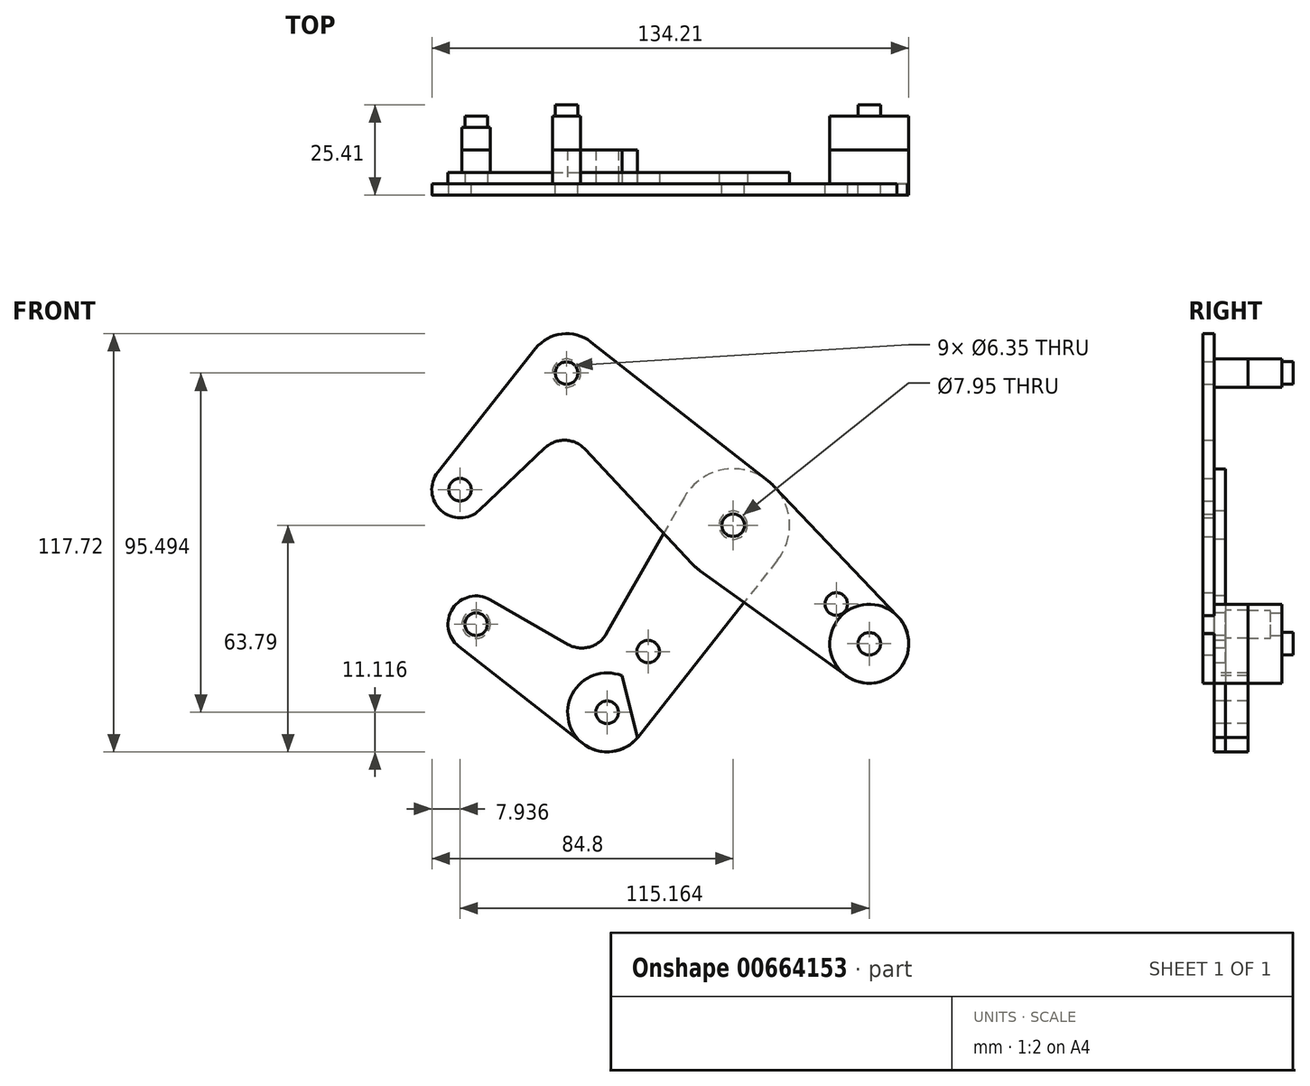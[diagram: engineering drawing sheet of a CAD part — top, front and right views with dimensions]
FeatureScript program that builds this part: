
annotation { "Feature Type Name" : "Feature", "Feature Type Description" : "" }
export const myFeature = defineFeature(function(context is Context, id is Id, definition is map)
    precondition{}
    {
        {
            var Q0;
            Q0=qCreatedBy(makeId("Front.planeOp"),FACE);
            var sketch = newSketch(context, id + "F0", { "sketchPlane" : qUnion([Q0])});
            skCircle(sketch, "E0", {"center": v(0, 0) * mm, "radius": 15.88 * mm});
            skCircle(sketch, "E1", {"center": v(-46.9, 42.82) * mm, "radius": 11.11 * mm});
            skCircle(sketch, "E2", {"center": v(-76.86, 10) * mm, "radius": 7.94 * mm});
            skCircle(sketch, "E3", {"center": v(38.3, -33.37) * mm, "radius": 11.11 * mm});
            skLineSegment(sketch, "E4", {"start": v(-46.9, 42.82) * mm, "end": v(37.51, -34.26) * mm, "construction": true});
            skLineSegment(sketch, "E5", {"start": v(-46.9, 42.82) * mm, "end": v(-76.86, 10) * mm, "construction": true});
            skCircle(sketch, "E6", {"center": v(0, 0) * mm, "radius": 3.98 * mm});
            skCircle(sketch, "E7", {"center": v(0, 0) * mm, "radius": 3.18 * mm});
            skCircle(sketch, "E8", {"center": v(-46.9, 42.82) * mm, "radius": 3.18 * mm});
            skCircle(sketch, "E9", {"center": v(-76.86, 10) * mm, "radius": 3.18 * mm});
            skCircle(sketch, "E10", {"center": v(38.3, -33.37) * mm, "radius": 3.18 * mm});
            skCircle(sketch, "E11", {"center": v(29.01, -22.2) * mm, "radius": 3.18 * mm});
            skLineSegment(sketch, "E12", {"start": v(26.87, -24.54) * mm, "end": v(46.56, -42.52) * mm, "construction": true});
            skLineSegment(sketch, "E13", {"start": v(0, 0) * mm, "end": v(-35.46, -52.67) * mm, "construction": true});
            skCircle(sketch, "E14", {"center": v(-35.46, -52.67) * mm, "radius": 11.11 * mm});
            skCircle(sketch, "E15", {"center": v(-35.46, -52.67) * mm, "radius": 3.18 * mm});
            skLineSegment(sketch, "E16", {"start": v(-35.46, -52.67) * mm, "end": v(-72.34, -27.85) * mm, "construction": true});
            skCircle(sketch, "E17", {"center": v(-72.34, -27.85) * mm, "radius": 7.94 * mm});
            skCircle(sketch, "E18", {"center": v(-72.34, -27.85) * mm, "radius": 3.18 * mm});
            skCircle(sketch, "E19", {"center": v(-23.93, -35.54) * mm, "radius": 3.18 * mm});
            skLineSegment(sketch, "E20", {"start": v(-55.61, 49.7) * mm, "end": v(-83.1, 14.92) * mm});
            skLineSegment(sketch, "E21", {"start": v(11.5, 10.94) * mm, "end": v(46.35, -25.72) * mm});
            skLineSegment(sketch, "E22", {"start": v(31.82, -42.4) * mm, "end": v(-9.26, -12.9) * mm});
            skLineSegment(sketch, "E23", {"start": v(-11.6, -10.83) * mm, "end": v(-41.7, 21.43) * mm});
            skLineSegment(sketch, "E24", {"start": v(-71.4, 4.24) * mm, "end": v(-52.96, 21.74) * mm});
            skLineSegment(sketch, "E25", {"start": v(-40.03, 51.56) * mm, "end": v(9.8, 12.5) * mm});
            skArc(sketch, "E26", {"start": v(-41.7, 21.43) * mm, "mid": v(-47.26, 23.92) * mm, "end": v(-52.96, 21.74) * mm});
            skArc(sketch, "E27", {"start": v(-41.83, 21.56) * mm, "mid": v(-47.35, 23.93) * mm, "end": v(-52.96, 21.74) * mm});
            skLineSegment(sketch, "E28", {"start": v(-52.96, 21.74) * mm, "end": v(-52.91, 21.78) * mm});
            skLineSegment(sketch, "E29", {"start": v(-41.7, 21.43) * mm, "end": v(-41.7, 21.43) * mm});
            skLineSegment(sketch, "E30.trimOffspring", {"start": v(-54.4, 34.6) * mm, "end": v(-54.98, 35.2) * mm});
            skPoint(sketch, "E31", {"position": v(-52.96, 21.74) * mm});
            skPoint(sketch, "E32", {"position": v(-41.7, 21.43) * mm});
            skLineSegment(sketch, "E33", {"start": v(-77.23, -34.1) * mm, "end": v(-42.31, -61.42) * mm});
            skLineSegment(sketch, "E34", {"start": v(12.47, -9.83) * mm, "end": v(-26.74, -59.55) * mm});
            skLineSegment(sketch, "E35", {"start": v(26.87, -24.54) * mm, "end": v(29.01, -22.2) * mm, "construction": true});
            skLineSegment(sketch, "E36", {"start": v(-11.72, 10.7) * mm, "end": v(-11.94, 10.47) * mm});
            skPoint(sketch, "E37.orphan", {"position": v(-90.16, -4.57) * mm});
            skLineSegment(sketch, "E38", {"start": v(-68.38, -20.96) * mm, "end": v(-46.52, -33.51) * mm});
            skLineSegment(sketch, "E39", {"start": v(-13.8, 7.85) * mm, "end": v(-35.66, -30.55) * mm});
            skArc(sketch, "E40", {"start": v(-46.52, -33.51) * mm, "mid": v(-40.48, -34.29) * mm, "end": v(-35.66, -30.55) * mm});
            skLineSegment(sketch, "E41.trimOffspring", {"start": v(-44.7, -46.45) * mm, "end": v(-45.12, -47.18) * mm});
            skLineSegment(sketch, "E42.trimOffspring", {"start": v(-29.93, -43.04) * mm, "end": v(-29.24, -43.43) * mm});
            skSolve(sketch);
        }
        {
            var Q0;
            {var subQ5=sQuery(id+"F0.wireOp",EDGE,"E20");Q0=makeQuery(id+"F0.imprint","IMPRINT",FACE,{"disambiguationData":[TD([[makeQuery(id+"F0.imprint","IMPRINT",EDGE,{"derivedFrom":subQ5}),1.0]])]});}
            var Q1;
            Q1=makeQuery(id+"F0.imprint","IMPRINT",FACE,{"disambiguationData":[TD([[makeQuery(id+"F0.imprint","IMPRINT",EDGE,{"derivedFrom":sQuery(id+"F0.wireOp",EDGE,"E9")}),-1.0]])]});
            var Q2;
            Q2=makeQuery(id+"F0.imprint","IMPRINT",FACE,{"disambiguationData":[TD([[makeQuery(id+"F0.imprint","IMPRINT",EDGE,{"derivedFrom":sQuery(id+"F0.wireOp",EDGE,"E8")}),-1.0]])]});
            var Q3;
            Q3=makeQuery(id+"F0.imprint","IMPRINT",FACE,{"disambiguationData":[TD([[makeQuery(id+"F0.imprint","IMPRINT",EDGE,{"derivedFrom":sQuery(id+"F0.wireOp",EDGE,"E6")}),-1.0]])]});
            var Q4;
            {var subQ0=sQuery(id+"F0.wireOp",EDGE,"E23");var subQ1=sQuery(id+"F0.wireOp",EDGE,"E0");var subQ2=makeQuery(id+"F0.imprint","INTERSECT",VERTEX,{"derivedFrom":[subQ1,subQ0]});Q4=makeQuery(id+"F0.imprint","IMPRINT",FACE,{"disambiguationData":[TD([[makeQuery(id+"F0.imprint","IMPRINT",EDGE,{"disambiguationData":[TD([[subQ2,1.0]])],"derivedFrom":subQ1}),-1.0]])]});}
            var Q5;
            Q5=makeQuery(id+"F0.imprint","IMPRINT",FACE,{"disambiguationData":[TD([[makeQuery(id+"F0.imprint","IMPRINT",EDGE,{"derivedFrom":sQuery(id+"F0.wireOp",EDGE,"E11")}),-1.0]])]});
            var Q6;
            {var subQ0=sQuery(id+"F0.wireOp",EDGE,"E22");var subQ1=sQuery(id+"F0.wireOp",EDGE,"E0");var subQ2=makeQuery(id+"F0.imprint","INTERSECT",VERTEX,{"derivedFrom":[subQ1,subQ0]});Q6=makeQuery(id+"F0.imprint","IMPRINT",FACE,{"disambiguationData":[TD([[makeQuery(id+"F0.imprint","IMPRINT",EDGE,{"disambiguationData":[TD([[subQ2,-1.0]])],"derivedFrom":subQ1}),-1.0]])]});}
            var Q7;
            Q7=makeQuery(id+"F0.imprint","IMPRINT",FACE,{"disambiguationData":[TD([[makeQuery(id+"F0.imprint","IMPRINT",EDGE,{"derivedFrom":sQuery(id+"F0.wireOp",EDGE,"E10")}),-1.0]])]});
            var Q8;
            Q8=makeQuery(id+"F0.imprint","IMPRINT",FACE,{"disambiguationData":[TD([[makeQuery(id+"F0.imprint","IMPRINT",EDGE,{"derivedFrom":sQuery(id+"F0.wireOp",EDGE,"E6")}),1.0]])]});
            extrude(context, id + "F1", {"entities" : qUnion([Q0, Q1, Q2, Q3, Q4, Q5, Q6, Q7, Q8]), "depth" : 3.17 * mm, "offsetDistance" : 25.4 * mm});
        }
        {
            var Q0;
            Q0=makeQuery(id+"F0.imprint","IMPRINT",FACE,{"disambiguationData":[TD([[makeQuery(id+"F0.imprint","IMPRINT",EDGE,{"derivedFrom":sQuery(id+"F0.wireOp",EDGE,"E19")}),-1.0]])]});
            var Q1;
            {var subQ0=sQuery(id+"F0.wireOp",EDGE,"E22");var subQ1=sQuery(id+"F0.wireOp",EDGE,"E0");var subQ2=makeQuery(id+"F0.imprint","INTERSECT",VERTEX,{"derivedFrom":[subQ1,subQ0]});Q1=makeQuery(id+"F0.imprint","IMPRINT",FACE,{"disambiguationData":[TD([[makeQuery(id+"F0.imprint","IMPRINT",EDGE,{"disambiguationData":[TD([[subQ2,-1.0]])],"derivedFrom":subQ1}),-1.0]])]});}
            var Q2;
            {var subQ0=sQuery(id+"F0.wireOp",EDGE,"E23");var subQ1=sQuery(id+"F0.wireOp",EDGE,"E0");var subQ2=makeQuery(id+"F0.imprint","INTERSECT",VERTEX,{"derivedFrom":[subQ1,subQ0]});Q2=makeQuery(id+"F0.imprint","IMPRINT",FACE,{"disambiguationData":[TD([[makeQuery(id+"F0.imprint","IMPRINT",EDGE,{"disambiguationData":[TD([[subQ2,1.0]])],"derivedFrom":subQ1}),-1.0]])]});}
            var Q3;
            Q3=makeQuery(id+"F0.imprint","IMPRINT",FACE,{"disambiguationData":[TD([[makeQuery(id+"F0.imprint","IMPRINT",EDGE,{"derivedFrom":sQuery(id+"F0.wireOp",EDGE,"E6")}),-1.0]])]});
            var Q4;
            Q4=makeQuery(id+"F0.imprint","IMPRINT",FACE,{"disambiguationData":[TD([[makeQuery(id+"F0.imprint","IMPRINT",EDGE,{"derivedFrom":sQuery(id+"F0.wireOp",EDGE,"E15")}),-1.0]])]});
            var Q5;
            {var subQ0=sQuery(id+"F0.wireOp",EDGE,"3amZSNLC-43hP-8FI3-ZThT-5at0zfi7Zp9o");Q5=makeQuery(id+"F0.imprint","IMPRINT",FACE,{"disambiguationData":[TD([[makeQuery(id+"F0.imprint","IMPRINT",EDGE,{"derivedFrom":subQ0}),1.0]])]});}
            var Q6;
            {var subQ0=sQuery(id+"F0.wireOp",EDGE,"E33");Q6=makeQuery(id+"F0.imprint","IMPRINT",FACE,{"disambiguationData":[TD([[makeQuery(id+"F0.imprint","IMPRINT",EDGE,{"derivedFrom":subQ0}),1.0]])]});}
            var Q7;
            Q7=makeQuery(id+"F0.imprint","IMPRINT",FACE,{"disambiguationData":[TD([[makeQuery(id+"F0.imprint","IMPRINT",EDGE,{"derivedFrom":sQuery(id+"F0.wireOp",EDGE,"E18")}),-1.0]])]});
            extrude(context, id + "F2", {"entities" : qUnion([Q0, Q1, Q2, Q3, Q4, Q5, Q6, Q7]), "oppositeDirection" : true, "depth" : 3.17 * mm, "offsetDistance" : 25.4 * mm});
        }
        {
            var Q0;
            Q0=makeQuery(id+"F1.opExtrude","CAP_FACE",FACE,{"disambiguationData":[OSD([sQuery(id+"F0.wireOp",EDGE,"E0"),sQuery(id+"F0.wireOp",EDGE,"E1"),sQuery(id+"F0.wireOp",EDGE,"E2"),sQuery(id+"F0.wireOp",EDGE,"E3"),sQuery(id+"F0.wireOp",EDGE,"E7"),sQuery(id+"F0.wireOp",EDGE,"E8"),sQuery(id+"F0.wireOp",EDGE,"E9"),sQuery(id+"F0.wireOp",EDGE,"E10"),sQuery(id+"F0.wireOp",EDGE,"E11"),sQuery(id+"F0.wireOp",EDGE,"E20"),sQuery(id+"F0.wireOp",EDGE,"E21"),sQuery(id+"F0.wireOp",EDGE,"E22"),sQuery(id+"F0.wireOp",EDGE,"E23"),sQuery(id+"F0.wireOp",EDGE,"E24"),sQuery(id+"F0.wireOp",EDGE,"E25"),sQuery(id+"F0.wireOp",EDGE,"E27"),sQuery(id+"F0.wireOp",EDGE,"E28")])],"isStart":false});
            var sketch = newSketch(context, id + "F3", { "sketchPlane" : qUnion([Q0])});
            skCircle(sketch, "E43", {"center": v(-46.9, 42.82) * mm, "radius": 3.98 * mm});
            skCircle(sketch, "E44", {"center": v(0, 0) * mm, "radius": 3.98 * mm});
            skCircle(sketch, "E45", {"center": v(38.3, -33.37) * mm, "radius": 11.11 * mm});
            skSolve(sketch);
        }
        {
            var Q0;
            Q0=makeQuery(id+"F2.opExtrude","CAP_FACE",FACE,{"disambiguationData":[OSD([sQuery(id+"F0.wireOp",EDGE,"E0"),sQuery(id+"F0.wireOp",EDGE,"E6"),sQuery(id+"F0.wireOp",EDGE,"E14"),sQuery(id+"F0.wireOp",EDGE,"E15"),sQuery(id+"F0.wireOp",EDGE,"E17"),sQuery(id+"F0.wireOp",EDGE,"E18"),sQuery(id+"F0.wireOp",EDGE,"E19"),sQuery(id+"F0.wireOp",EDGE,"zHbHai0O-zoeY-vRAu-LCtb-dT5vAsICp8MH"),sQuery(id+"F0.wireOp",EDGE,"ZkpdVOQ3-HPfv-Rj2Q-2N2k-vu5tipJXAsQn"),sQuery(id+"F0.wireOp",EDGE,"E33"),sQuery(id+"F0.wireOp",EDGE,"E34"),sQuery(id+"F0.wireOp",EDGE,"qrG7Sbz3-pH1N-X5PJ-92qv-GuBl7YAv6E5Q"),sQuery(id+"F0.wireOp",EDGE,"3amZSNLC-43hP-8FI3-ZThT-5at0zfi7Zp9o")])],"isStart":true});
            var sketch = newSketch(context, id + "F4", { "sketchPlane" : qUnion([Q0])});
            skCircle(sketch, "E46", {"center": v(-35.46, -52.67) * mm, "radius": 11.11 * mm});
            skPoint(sketch, "E47", {"position": v(-29.11, -52.67) * mm});
            skLineSegment(sketch, "E48", {"start": v(-29.11, -43.55) * mm, "end": v(-29.11, -43.55) * mm});
            skCircle(sketch, "E49", {"center": v(-72.34, -27.85) * mm, "radius": 3.98 * mm});
            skLineSegment(sketch, "E50", {"start": v(-35.46, -52.67) * mm, "end": v(38.72, -33.99) * mm, "construction": true});
            skPoint(sketch, "E51", {"position": v(-29.11, -51.07) * mm});
            skLineSegment(sketch, "E52", {"start": v(-31.3, -42.37) * mm, "end": v(-29.11, -51.07) * mm});
            skLineSegment(sketch, "E53", {"start": v(-29.11, -51.07) * mm, "end": v(-26.92, -59.78) * mm});
            skSolve(sketch);
        }
        {
            var Q0;
            Q0=qCreatedBy(makeId("Front.planeOp"),FACE);
            cPlane(context, id + "F5", {"entities" : qUnion([Q0]), "cplaneType" : CPlaneType.OFFSET, "offset" : 9.52 * mm, "oppositeDirection" : true, "width" : 152.4 * mm, "height" : 152.4 * mm});
        }
        {
            var Q0;
            Q0=makeQuery(id+"F3.imprint","IMPRINT",FACE,{"disambiguationData":[TD([[makeQuery(id+"F3.imprint","IMPRINT",EDGE,{"derivedFrom":sQuery(id+"F3.wireOp",EDGE,"E43")}),1.0]])]});
            var Q1;
            Q1=makeQuery(id+"F4.imprint","IMPRINT",FACE,{"disambiguationData":[TD([[makeQuery(id+"F4.imprint","IMPRINT",EDGE,{"derivedFrom":makeQuery(id+"F2.opExtrude","CAP_EDGE",EDGE,{"disambiguationData":[OSD([sQuery(id+"F0.wireOp",EDGE,"E18")])],"isStart":true})}),1.0]])]});
            var Q2;
            Q2=makeQuery(id+"F4.imprint","IMPRINT",FACE,{"disambiguationData":[TD([[makeQuery(id+"F4.imprint","IMPRINT",EDGE,{"derivedFrom":sQuery(id+"F4.wireOp",EDGE,"E49")}),1.0]])]});
            var Q3;
            Q3=makeQuery(id+"F3.imprint","IMPRINT",FACE,{"disambiguationData":[TD([[makeQuery(id+"F3.imprint","IMPRINT",EDGE,{"derivedFrom":makeQuery(id+"F1.opExtrude","CAP_EDGE",EDGE,{"disambiguationData":[OSD([sQuery(id+"F0.wireOp",EDGE,"E8")])],"isStart":false})}),1.0]])]});
            var Q4;
            Q4=makeQuery(id+"F4.imprint","IMPRINT",FACE,{"disambiguationData":[TD([[makeQuery(id+"F4.imprint","IMPRINT",EDGE,{"derivedFrom":makeQuery(id+"F2.opExtrude","CAP_EDGE",EDGE,{"disambiguationData":[OSD([sQuery(id+"F0.wireOp",EDGE,"E15")])],"isStart":true})}),1.0]])]});
            var Q5;
            {var subQ2=sQuery(id+"F4.wireOp",EDGE,"E48");Q5=makeQuery(id+"F4.imprint","IMPRINT",FACE,{"disambiguationData":[TD([[makeQuery(id+"F4.imprint","IMPRINT",EDGE,{"derivedFrom":subQ2}),-1.0]])]});}
            var Q6;
            Q6=qCreatedBy(id+"F5.planeOp",FACE);
            extrude(context, id + "F6", {"entities" : qUnion([Q0, Q1, Q2, Q3, Q4, Q5]), "endBound" : BoundingType.UP_TO_SURFACE, "oppositeDirection" : true, "depth" : 25.4 * mm, "endBoundEntityFace" : qUnion([Q6]), "offsetDistance" : 25.4 * mm});
        }
        {
            var Q0;
            Q0=makeQuery(id+"F1.opExtrude","SWEPT_BODY",BODY,{"disambiguationData":[OSD([sQuery(id+"F0.wireOp",EDGE,"E0"),sQuery(id+"F0.wireOp",EDGE,"E1"),sQuery(id+"F0.wireOp",EDGE,"E2"),sQuery(id+"F0.wireOp",EDGE,"E3"),sQuery(id+"F0.wireOp",EDGE,"E7"),sQuery(id+"F0.wireOp",EDGE,"E8"),sQuery(id+"F0.wireOp",EDGE,"E9"),sQuery(id+"F0.wireOp",EDGE,"E10"),sQuery(id+"F0.wireOp",EDGE,"E11"),sQuery(id+"F0.wireOp",EDGE,"E20"),sQuery(id+"F0.wireOp",EDGE,"E21"),sQuery(id+"F0.wireOp",EDGE,"E22"),sQuery(id+"F0.wireOp",EDGE,"E23"),sQuery(id+"F0.wireOp",EDGE,"E24"),sQuery(id+"F0.wireOp",EDGE,"E25"),sQuery(id+"F0.wireOp",EDGE,"E27"),sQuery(id+"F0.wireOp",EDGE,"E28")])]});
            var Q1;
            Q1=makeQuery(id+"F2.opExtrude","SWEPT_BODY",BODY,{"disambiguationData":[OSD([sQuery(id+"F0.wireOp",EDGE,"E0"),sQuery(id+"F0.wireOp",EDGE,"E6"),sQuery(id+"F0.wireOp",EDGE,"E14"),sQuery(id+"F0.wireOp",EDGE,"E15"),sQuery(id+"F0.wireOp",EDGE,"E17"),sQuery(id+"F0.wireOp",EDGE,"E18"),sQuery(id+"F0.wireOp",EDGE,"E19"),sQuery(id+"F0.wireOp",EDGE,"zHbHai0O-zoeY-vRAu-LCtb-dT5vAsICp8MH"),sQuery(id+"F0.wireOp",EDGE,"ZkpdVOQ3-HPfv-Rj2Q-2N2k-vu5tipJXAsQn"),sQuery(id+"F0.wireOp",EDGE,"E33"),sQuery(id+"F0.wireOp",EDGE,"E34"),sQuery(id+"F0.wireOp",EDGE,"qrG7Sbz3-pH1N-X5PJ-92qv-GuBl7YAv6E5Q"),sQuery(id+"F0.wireOp",EDGE,"3amZSNLC-43hP-8FI3-ZThT-5at0zfi7Zp9o")])]});
            var Q2;
            Q2=makeQuery(id+"F6.opExtrude","SWEPT_BODY",BODY,{"disambiguationData":[OSD([sQuery(id+"F3.wireOp",EDGE,"E43")])]});
            var Q3;
            Q3=makeQuery(id+"F6.opExtrude","SWEPT_BODY",BODY,{"disambiguationData":[OSD([sQuery(id+"F4.wireOp",EDGE,"E49")])]});
            var Q4;
            Q4=makeQuery(id+"F6.opExtrude","SWEPT_BODY",BODY,{"disambiguationData":[OSD([sQuery(id+"F4.wireOp",EDGE,"E46"),sQuery(id+"F4.wireOp",EDGE,"E48")])]});
            booleanBodies(context, id + "F7", {"operationType" : BooleanOperationType.SUBTRACTION, "tools" : qUnion([Q0, Q1]), "targets" : qUnion([Q2, Q3, Q4]), "keepTools" : true});
        }
        {
            var Q0;
            Q0=makeQuery(id+"F3.imprint","IMPRINT",FACE,{"disambiguationData":[TD([[makeQuery(id+"F3.imprint","IMPRINT",EDGE,{"derivedFrom":makeQuery(id+"F1.opExtrude","CAP_EDGE",EDGE,{"disambiguationData":[OSD([sQuery(id+"F0.wireOp",EDGE,"E10")])],"isStart":false})}),-1.0]])]});
            cPlane(context, id + "F8", {"entities" : qUnion([Q0]), "cplaneType" : CPlaneType.OFFSET, "offset" : 0 * mm, "width" : 152.4 * mm, "height" : 152.4 * mm});
        }
        {
            var Q0;
            Q0=qCreatedBy(id+"F8.planeOp",FACE);
            var sketch = newSketch(context, id + "F9", { "sketchPlane" : qUnion([Q0])});
            skCircle(sketch, "E54", {"center": v(38.3, -33.36) * mm, "radius": 11.11 * mm});
            skSolve(sketch);
        }
        {
            var Q0;
            Q0=qSketchRegion(id+"F9",true);
            var Q1;
            Q1=qCreatedBy(id+"F5.planeOp",FACE);
            extrude(context, id + "F10", {"entities" : qUnion([Q0]), "endBound" : BoundingType.UP_TO_SURFACE, "oppositeDirection" : true, "depth" : 16.5 * mm, "endBoundEntityFace" : qUnion([Q1]), "offsetDistance" : 25.4 * mm});
        }
        {
            var Q0;
            Q0=makeQuery(id+"F1.opExtrude","SWEPT_BODY",BODY,{"disambiguationData":[OSD([sQuery(id+"F0.wireOp",EDGE,"E0"),sQuery(id+"F0.wireOp",EDGE,"E1"),sQuery(id+"F0.wireOp",EDGE,"E2"),sQuery(id+"F0.wireOp",EDGE,"E3"),sQuery(id+"F0.wireOp",EDGE,"E7"),sQuery(id+"F0.wireOp",EDGE,"E8"),sQuery(id+"F0.wireOp",EDGE,"E9"),sQuery(id+"F0.wireOp",EDGE,"E10"),sQuery(id+"F0.wireOp",EDGE,"E11"),sQuery(id+"F0.wireOp",EDGE,"E20"),sQuery(id+"F0.wireOp",EDGE,"E21"),sQuery(id+"F0.wireOp",EDGE,"E22"),sQuery(id+"F0.wireOp",EDGE,"E23"),sQuery(id+"F0.wireOp",EDGE,"E24"),sQuery(id+"F0.wireOp",EDGE,"E25"),sQuery(id+"F0.wireOp",EDGE,"E27"),sQuery(id+"F0.wireOp",EDGE,"E28")])]});
            var Q1;
            Q1=makeQuery(id+"F10.opExtrude","SWEPT_BODY",BODY,{"disambiguationData":[OSD([sQuery(id+"F9.wireOp",EDGE,"E54")])]});
            booleanBodies(context, id + "F11", {"operationType" : BooleanOperationType.SUBTRACTION, "tools" : qUnion([Q0]), "targets" : qUnion([Q1]), "keepTools" : true});
        }
        {
            var Q0;
            Q0=makeQuery(id+"F6.opExtrude","SWEPT_BODY",BODY,{"disambiguationData":[OSD([sQuery(id+"F4.wireOp",EDGE,"E46"),sQuery(id+"F4.wireOp",EDGE,"E48")])]});
            var Q1;
            Q1=makeQuery(id+"F10.opExtrude","SWEPT_BODY",BODY,{"disambiguationData":[OSD([sQuery(id+"F9.wireOp",EDGE,"E54")])]});
            var Q2;
            Q2=makeQuery(id+"F6.opExtrude","SWEPT_BODY",BODY,{"disambiguationData":[OSD([sQuery(id+"F3.wireOp",EDGE,"E43")])]});
            var Q3;
            Q3=makeQuery(id+"F6.opExtrude","SWEPT_BODY",BODY,{"disambiguationData":[OSD([sQuery(id+"F4.wireOp",EDGE,"E49")])]});
            var Q4;
            Q4=qCreatedBy(id+"F5.planeOp",FACE);
            mirror(context, id + "F12", {"entities" : qUnion([Q0, Q1, Q2, Q3]), "mirrorPlane" : qUnion([Q4])});
        }
        {
            var Q0;
            Q0=makeQuery(id+"F12.opPattern","COPY",FACE,{"derivedFrom":makeQuery(id+"F11.opBoolean","COPY",FACE,{"derivedFrom":makeQuery(id+"F1.opExtrude","CAP_FACE",FACE,{"disambiguationData":[OSD([sQuery(id+"F0.wireOp",EDGE,"E0"),sQuery(id+"F0.wireOp",EDGE,"E1"),sQuery(id+"F0.wireOp",EDGE,"E2"),sQuery(id+"F0.wireOp",EDGE,"E3"),sQuery(id+"F0.wireOp",EDGE,"E7"),sQuery(id+"F0.wireOp",EDGE,"E8"),sQuery(id+"F0.wireOp",EDGE,"E9"),sQuery(id+"F0.wireOp",EDGE,"E10"),sQuery(id+"F0.wireOp",EDGE,"E11"),sQuery(id+"F0.wireOp",EDGE,"E20"),sQuery(id+"F0.wireOp",EDGE,"E21"),sQuery(id+"F0.wireOp",EDGE,"E22"),sQuery(id+"F0.wireOp",EDGE,"E23"),sQuery(id+"F0.wireOp",EDGE,"E24"),sQuery(id+"F0.wireOp",EDGE,"E25"),sQuery(id+"F0.wireOp",EDGE,"E27"),sQuery(id+"F0.wireOp",EDGE,"E28")])],"isStart":true})}),"instanceName":"1"});
            var sketch = newSketch(context, id + "F13", { "sketchPlane" : qUnion([Q0])});
            skLineSegment(sketch, "E55.bottom", {"start": v(-45.55, -34.91) * mm, "end": v(-56.4, -34.91) * mm});
            skLineSegment(sketch, "E55.top", {"start": v(-45.55, -18.05) * mm, "end": v(-56.4, -18.05) * mm});
            skLineSegment(sketch, "E55.left", {"start": v(-45.55, -34.91) * mm, "end": v(-45.55, -18.05) * mm});
            skLineSegment(sketch, "E55.right", {"start": v(-56.4, -34.91) * mm, "end": v(-56.4, -18.05) * mm});
            skSolve(sketch);
        }
        {
            var Q0;
            Q0=qSketchRegion(id+"F13",true);
            extrude(context, id + "F14", {"entities" : qUnion([Q0]), "operationType" : NewBodyOperationType.REMOVE, "depth" : 25.4 * mm, "offsetDistance" : 25.4 * mm});
        }
        {
            var Q0;
            {var subQ3=sQuery(id+"F4.wireOp",EDGE,"E52");Q0=makeQuery(id+"F4.imprint","IMPRINT",FACE,{"disambiguationData":[TD([[makeQuery(id+"F4.imprint","IMPRINT",EDGE,{"derivedFrom":subQ3}),-1.0]])]});}
            var Q1;
            Q1=qCreatedBy(id+"F5.planeOp",FACE);
            extrude(context, id + "F15", {"entities" : qUnion([Q0]), "endBound" : BoundingType.UP_TO_SURFACE, "oppositeDirection" : true, "depth" : 25.4 * mm, "endBoundEntityFace" : qUnion([Q1]), "offsetDistance" : 25.4 * mm});
        }
    });
